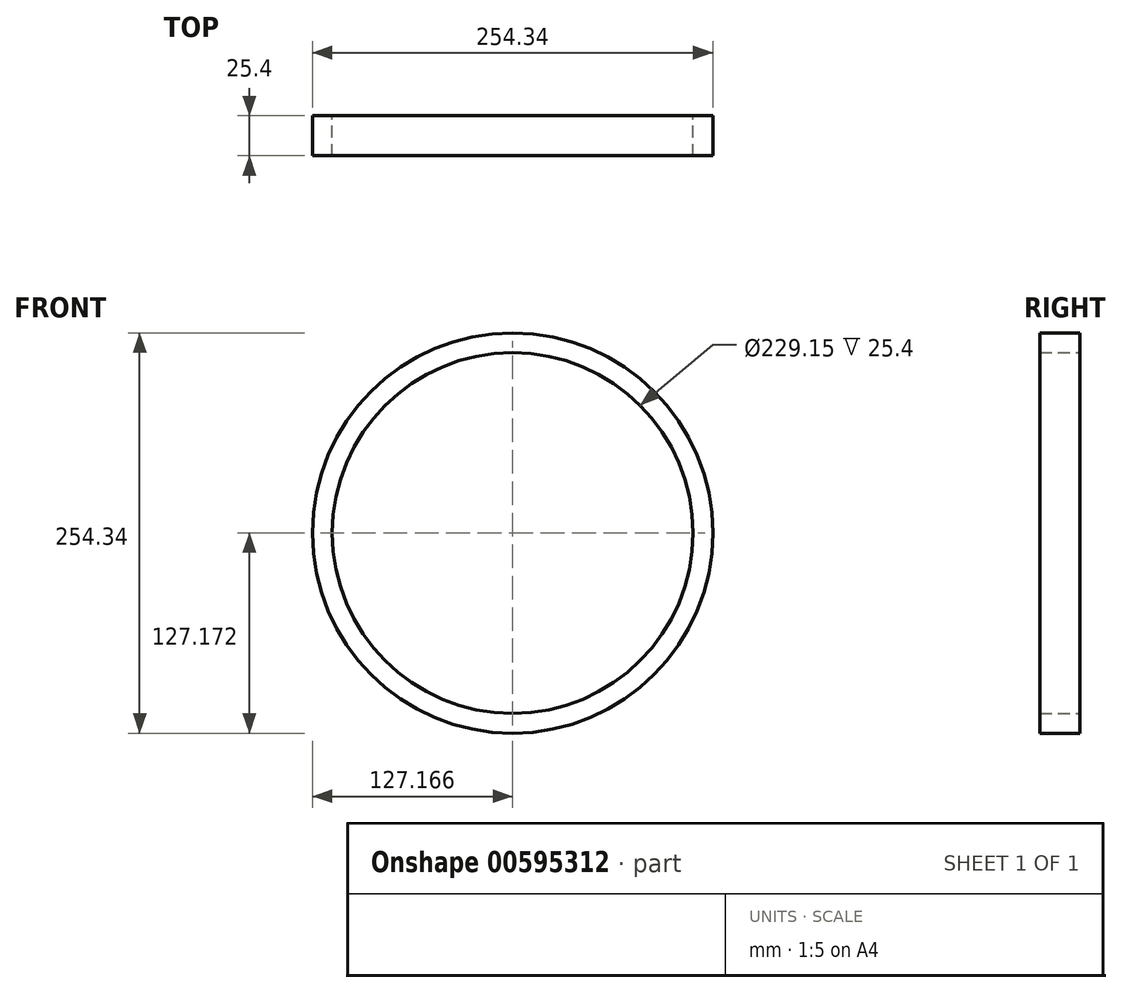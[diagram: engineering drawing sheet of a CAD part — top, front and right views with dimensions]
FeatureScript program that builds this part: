
annotation { "Feature Type Name" : "Feature", "Feature Type Description" : "" }
export const myFeature = defineFeature(function(context is Context, id is Id, definition is map)
    precondition{}
    {
        {
            var Q0;
            Q0=qCreatedBy(makeId("Front.planeOp"),FACE);
            var sketch = newSketch(context, id + "F0", { "sketchPlane" : qUnion([Q0])});
            skCircle(sketch, "E0", {"center": v(-156.56, 116.23) * mm, "radius": 127.17 * mm});
            skCircle(sketch, "E1", {"center": v(-156.56, 116.23) * mm, "radius": 114.57 * mm});
            skSolve(sketch);
        }
        {
            var Q0;
            Q0=makeQuery(id+"F0.imprint","IMPRINT",FACE,{"disambiguationData":[TD([[makeQuery(id+"F0.imprint","IMPRINT",EDGE,{"derivedFrom":sQuery(id+"F0.wireOp",EDGE,"E0")}),1.0]])]});
            extrude(context, id + "F1", {"entities" : qUnion([Q0]), "depth" : 25.4 * mm, "offsetDistance" : 25.4 * mm});
        }
    });
